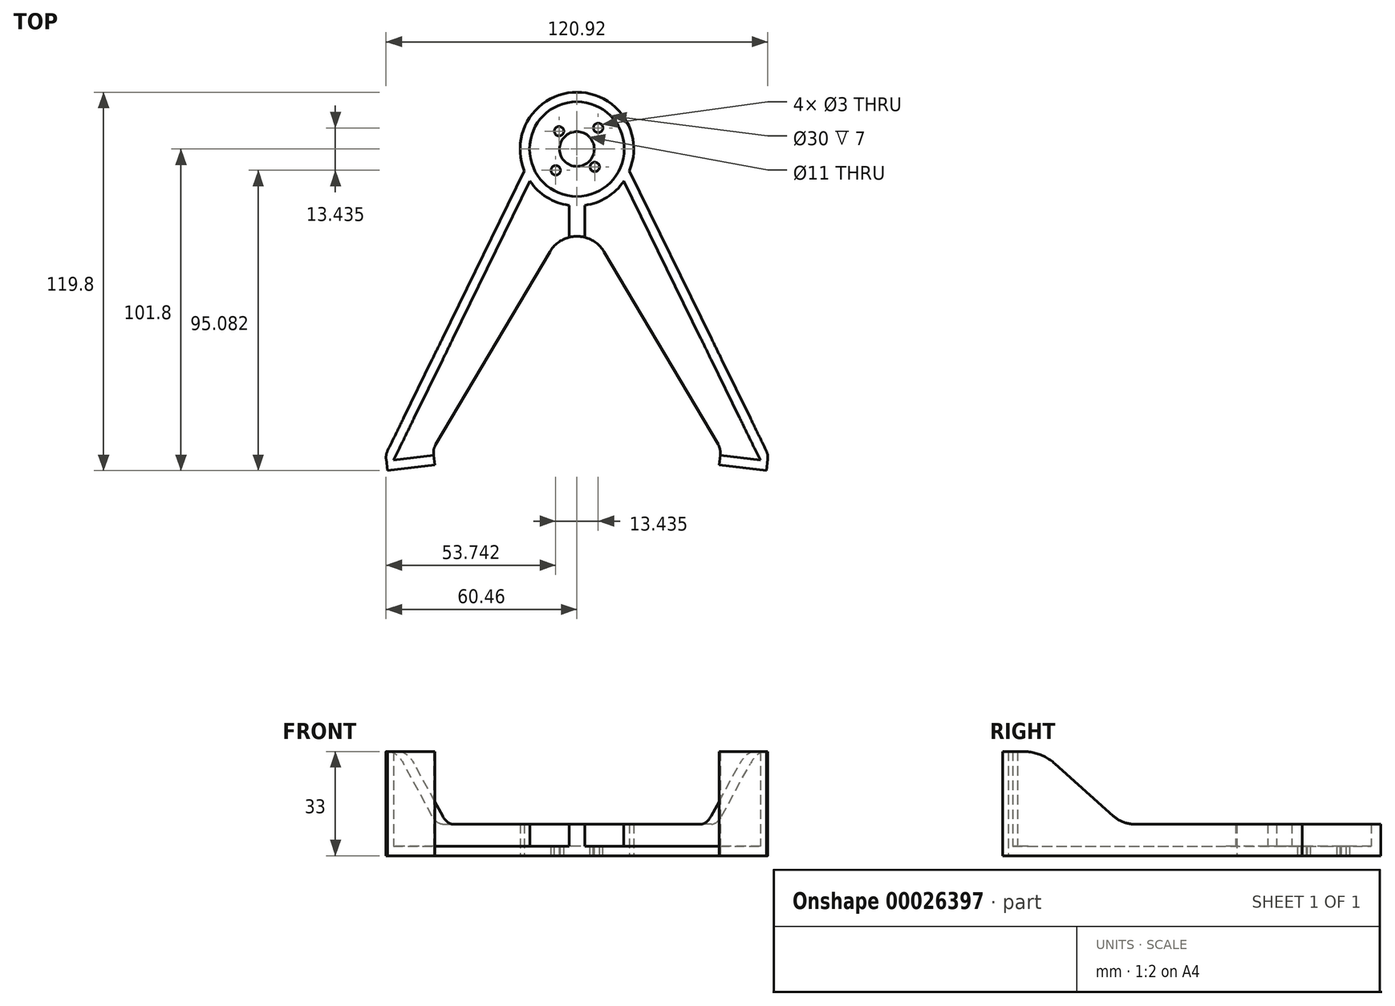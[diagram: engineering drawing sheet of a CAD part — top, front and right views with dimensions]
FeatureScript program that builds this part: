
annotation { "Feature Type Name" : "Feature", "Feature Type Description" : "" }
export const myFeature = defineFeature(function(context is Context, id is Id, definition is map)
    precondition{}
    {
        {
            var Q0;
            Q0=qCreatedBy(makeId("Top.planeOp"),FACE);
            var sketch = newSketch(context, id + "F0", { "sketchPlane" : qUnion([Q0])});
            skLineSegment(sketch, "E0", {"start": v(45, 0) * mm, "end": v(60, -1.8) * mm});
            skCircle(sketch, "E1", {"center": v(0, 100) * mm, "radius": 15 * mm});
            skCircle(sketch, "E2", {"center": v(0, 100) * mm, "radius": 18 * mm});
            skLineSegment(sketch, "E3", {"start": v(60, -1.8) * mm, "end": v(60.42, 1.7) * mm});
            skLineSegment(sketch, "E4", {"start": v(59.95, 4.5) * mm, "end": v(16.63, 93.11) * mm});
            skLineSegment(sketch, "E5", {"start": v(44.73, 6.42) * mm, "end": v(8.6, 67.46) * mm});
            skLineSegment(sketch, "E6.MirrorCS", {"start": v(-45.6, 4.96) * mm, "end": v(-8.6, 67.46) * mm});
            skLineSegment(sketch, "E7.MirrorCS", {"start": v(-45, 0) * mm, "end": v(-60, -1.8) * mm});
            skLineSegment(sketch, "E8.MirrorCS", {"start": v(-60, -1.8) * mm, "end": v(-60.42, 1.7) * mm});
            skLineSegment(sketch, "E9.MirrorCS", {"start": v(-59.95, 4.5) * mm, "end": v(-16.63, 93.11) * mm});
            skArc(sketch, "E10", {"start": v(8.6, 67.46) * mm, "mid": v(0, 72.37) * mm, "end": v(-8.6, 67.46) * mm});
            skPoint(sketch, "E11.orphan", {"position": v(0, 82) * mm});
            skPoint(sketch, "E12.visualSharp", {"position": v(-60.6, 3.16) * mm});
            skArc(sketch, "E12.filletArc", {"start": v(-59.95, 4.5) * mm, "mid": v(-60.39, 3.13) * mm, "end": v(-60.42, 1.7) * mm});
            skPoint(sketch, "E13.visualSharp", {"position": v(60.6, 3.16) * mm});
            skArc(sketch, "E13.filletArc", {"start": v(60.42, 1.7) * mm, "mid": v(60.39, 3.13) * mm, "end": v(59.95, 4.5) * mm});
            skLineSegment(sketch, "E14", {"start": v(45, 0) * mm, "end": v(45.4, 3.28) * mm});
            skPoint(sketch, "E15.visualSharp", {"position": v(45.6, 4.96) * mm});
            skArc(sketch, "E15.filletArc", {"start": v(45.4, 3.28) * mm, "mid": v(45.32, 4.9) * mm, "end": v(44.73, 6.42) * mm});
            skLineSegment(sketch, "E16.MirrorCS", {"start": v(-45, 0) * mm, "end": v(-45.4, 3.28) * mm});
            skArc(sketch, "E17.MirrorCS", {"start": v(-45.4, 3.28) * mm, "mid": v(-45.32, 4.9) * mm, "end": v(-44.73, 6.42) * mm});
            skSolve(sketch);
        }
        {
            var Q0;
            Q0=makeQuery(id+"F0.imprint","IMPRINT",FACE,{"disambiguationData":[TD([[makeQuery(id+"F0.imprint","IMPRINT",EDGE,{"derivedFrom":sQuery(id+"F0.wireOp",EDGE,"E0")}),1.0]])]});
            var Q1;
            Q1=makeQuery(id+"F0.imprint","IMPRINT",FACE,{"disambiguationData":[TD([[makeQuery(id+"F0.imprint","IMPRINT",EDGE,{"derivedFrom":sQuery(id+"F0.wireOp",EDGE,"E1")}),-1.0]])]});
            var Q2;
            Q2=makeQuery(id+"F0.imprint","IMPRINT",FACE,{"disambiguationData":[TD([[makeQuery(id+"F0.imprint","IMPRINT",EDGE,{"derivedFrom":sQuery(id+"F0.wireOp",EDGE,"E1")}),1.0]])]});
            extrude(context, id + "F1", {"entities" : qUnion([Q0, Q1, Q2]), "depth" : 3 * mm});
        }
        {
            var Q0;
            Q0=makeQuery(id+"F0.imprint","IMPRINT",FACE,{"disambiguationData":[TD([[makeQuery(id+"F0.imprint","IMPRINT",EDGE,{"derivedFrom":sQuery(id+"F0.wireOp",EDGE,"E1")}),-1.0]])]});
            extrude(context, id + "F2", {"entities" : qUnion([Q0]), "operationType" : NewBodyOperationType.ADD, "depth" : 10 * mm});
        }
        {
            var Q0;
            {var subQ0=sQuery(id+"F0.wireOp",EDGE,"E10");var subQ1=sQuery(id+"F0.wireOp",EDGE,"E8.MirrorCS");var subQ2=sQuery(id+"F0.wireOp",EDGE,"E16.MirrorCS");var subQ3=sQuery(id+"F0.wireOp",EDGE,"E7.MirrorCS");var subQ4=sQuery(id+"F0.wireOp",EDGE,"E6.MirrorCS");var subQ5=sQuery(id+"F0.wireOp",EDGE,"E5");var subQ6=sQuery(id+"F0.wireOp",EDGE,"E0");var subQ7=sQuery(id+"F0.wireOp",EDGE,"E9.MirrorCS");var subQ8=sQuery(id+"F0.wireOp",EDGE,"E17.MirrorCS");var subQ9=sQuery(id+"F0.wireOp",EDGE,"E2");var subQ10=sQuery(id+"F0.wireOp",EDGE,"E3");var subQ11=sQuery(id+"F0.wireOp",EDGE,"E4");var subQ12=sQuery(id+"F0.wireOp",EDGE,"E12.filletArc");var subQ13=sQuery(id+"F0.wireOp",EDGE,"E13.filletArc");var subQ14=sQuery(id+"F0.wireOp",EDGE,"E14");var subQ15=sQuery(id+"F0.wireOp",EDGE,"E15.filletArc");Q0=makeQuery(id+"F2.boolean.opBoolean","SPLIT",FACE,{"disambiguationData":[TD([makeQuery(id+"F1.opExtrude","SWEPT_FACE",FACE,{"disambiguationData":[OSD([subQ6])]})])],"derivedFrom":makeQuery(id+"F1.opExtrude","CAP_FACE",FACE,{"disambiguationData":[OSD([subQ6,subQ9,subQ10,subQ11,subQ5,subQ4,subQ3,subQ1,subQ7,subQ0,subQ12,subQ13,subQ14,subQ15,subQ2,subQ8])],"isStart":false})});}
            var sketch = newSketch(context, id + "F3", { "sketchPlane" : qUnion([Q0])});
            skLineSegment(sketch, "E18.0", {"start": v(-58.1, 1.45) * mm, "end": v(-14.88, 89.87) * mm});
            skLineSegment(sketch, "E18.1", {"start": v(-45.36, 2.98) * mm, "end": v(-58.1, 1.45) * mm});
            skLineSegment(sketch, "E19", {"start": v(-58.1, 1.45) * mm, "end": v(-60.36, 1.18) * mm});
            skLineSegment(sketch, "E20.MirrorCS", {"start": v(45.36, 2.98) * mm, "end": v(58.1, 1.45) * mm});
            skLineSegment(sketch, "E21.MirrorCS", {"start": v(58.1, 1.45) * mm, "end": v(14.88, 89.87) * mm});
            skLineSegment(sketch, "E22.MirrorCS", {"start": v(58.1, 1.45) * mm, "end": v(60.36, 1.18) * mm});
            skCircle(sketch, "E23.0", {"center": v(0, 100) * mm, "radius": 18 * mm});
            skLineSegment(sketch, "E24.0", {"start": v(-59.95, 4.5) * mm, "end": v(-16.63, 93.11) * mm});
            skArc(sketch, "E25.0", {"start": v(-59.95, 4.5) * mm, "mid": v(-60.39, 3.13) * mm, "end": v(-60.42, 1.7) * mm});
            skLineSegment(sketch, "E26.0", {"start": v(-60, -1.8) * mm, "end": v(-60.42, 1.7) * mm});
            skLineSegment(sketch, "E27.0", {"start": v(-45, 0) * mm, "end": v(-60, -1.8) * mm});
            skLineSegment(sketch, "E28.0", {"start": v(-45, 0) * mm, "end": v(-45.4, 3.28) * mm});
            skLineSegment(sketch, "E29.0", {"start": v(45, 0) * mm, "end": v(45.4, 3.28) * mm});
            skLineSegment(sketch, "E30.0", {"start": v(45, 0) * mm, "end": v(60, -1.8) * mm});
            skLineSegment(sketch, "E31.0", {"start": v(60, -1.8) * mm, "end": v(60.42, 1.7) * mm});
            skArc(sketch, "E32.0", {"start": v(60.42, 1.7) * mm, "mid": v(60.39, 3.13) * mm, "end": v(59.95, 4.5) * mm});
            skLineSegment(sketch, "E33.0", {"start": v(59.95, 4.5) * mm, "end": v(16.63, 93.11) * mm});
            skSolve(sketch);
        }
        {
            var Q0;
            {var subQ2=sQuery(id+"F3.wireOp",EDGE,"E18.0");Q0=makeQuery(id+"F3.imprint","IMPRINT",FACE,{"disambiguationData":[TD([[makeQuery(id+"F3.imprint","IMPRINT",EDGE,{"derivedFrom":subQ2}),1.0]])]});}
            var Q1;
            {var subQ5=sQuery(id+"F3.wireOp",EDGE,"E21.MirrorCS");Q1=makeQuery(id+"F3.imprint","IMPRINT",FACE,{"disambiguationData":[TD([[makeQuery(id+"F3.imprint","IMPRINT",EDGE,{"derivedFrom":subQ5}),-1.0]])]});}
            var Q2;
            Q2=makeQuery(id+"F2.opExtrude","CAP_FACE",FACE,{"disambiguationData":[OSD([sQuery(id+"F0.wireOp",EDGE,"E1"),sQuery(id+"F0.wireOp",EDGE,"E2")])],"isStart":false});
            extrude(context, id + "F4", {"entities" : qUnion([Q0, Q1]), "operationType" : NewBodyOperationType.ADD, "endBound" : BoundingType.UP_TO_SURFACE, "endBoundEntityFace" : qUnion([Q2]), "depth" : 7 * mm});
        }
        {
            var Q0;
            {var subQ3=sQuery(id+"F3.wireOp",EDGE,"E18.1");Q0=makeQuery(id+"F3.imprint","IMPRINT",FACE,{"disambiguationData":[TD([[makeQuery(id+"F3.imprint","IMPRINT",EDGE,{"derivedFrom":subQ3}),1.0]])]});}
            var Q1;
            {var subQ2=sQuery(id+"F3.wireOp",EDGE,"E20.MirrorCS");Q1=makeQuery(id+"F3.imprint","IMPRINT",FACE,{"disambiguationData":[TD([[makeQuery(id+"F3.imprint","IMPRINT",EDGE,{"derivedFrom":subQ2}),-1.0]])]});}
            extrude(context, id + "F5", {"entities" : qUnion([Q0, Q1]), "operationType" : NewBodyOperationType.ADD, "depth" : 30 * mm});
        }
        {
            var Q0;
            {var subQ7=sQuery(id+"F3.wireOp",EDGE,"E18.0");Q0=makeQuery(id+"F3.imprint","IMPRINT",FACE,{"disambiguationData":[TD([[makeQuery(id+"F3.imprint","IMPRINT",EDGE,{"derivedFrom":subQ7}),-1.0]])]});}
            var sketch = newSketch(context, id + "F6", { "sketchPlane" : qUnion([Q0])});
            skArc(sketch, "E34.0", {"start": v(-14.88, 89.87) * mm, "mid": v(0, 82) * mm, "end": v(14.88, 89.87) * mm});
            skArc(sketch, "E35.0", {"start": v(8.6, 67.46) * mm, "mid": v(0, 72.37) * mm, "end": v(-8.6, 67.46) * mm});
            skLineSegment(sketch, "E36", {"start": v(-2.5, 82.17) * mm, "end": v(-2.5, 72.05) * mm});
            skLineSegment(sketch, "E37.MirrorCS", {"start": v(2.5, 82.17) * mm, "end": v(2.5, 72.05) * mm});
            skSolve(sketch);
        }
        {
            var Q0;
            {var subQ0=sQuery(id+"F6.wireOp",EDGE,"E36");Q0=makeQuery(id+"F6.imprint","IMPRINT",FACE,{"disambiguationData":[TD([[makeQuery(id+"F6.imprint","IMPRINT",EDGE,{"derivedFrom":subQ0}),1.0]])]});}
            var Q1;
            {var subQ0=sQuery(id+"F3.wireOp",EDGE,"E23.0");Q1=makeQuery(id+"F4.boolean.opBoolean","MERGE",FACE,{"derivedFrom":[makeQuery(id+"F2.opExtrude","CAP_FACE",FACE,{"disambiguationData":[OSD([sQuery(id+"F0.wireOp",EDGE,"E1"),sQuery(id+"F0.wireOp",EDGE,"E2")])],"isStart":false}),makeQuery(id+"F4.opExtrude","CAP_FACE",FACE,{"disambiguationData":[OSD([sQuery(id+"F3.wireOp",EDGE,"E18.0"),sQuery(id+"F3.wireOp",EDGE,"E19"),subQ0,sQuery(id+"F3.wireOp",EDGE,"E24.0"),sQuery(id+"F3.wireOp",EDGE,"E25.0"),sQuery(id+"F3.wireOp",EDGE,"E26.0")])],"isStart":false}),makeQuery(id+"F4.opExtrude","CAP_FACE",FACE,{"disambiguationData":[OSD([sQuery(id+"F3.wireOp",EDGE,"E21.MirrorCS"),sQuery(id+"F3.wireOp",EDGE,"E22.MirrorCS"),subQ0,sQuery(id+"F3.wireOp",EDGE,"E31.0"),sQuery(id+"F3.wireOp",EDGE,"E32.0"),sQuery(id+"F3.wireOp",EDGE,"E33.0")])],"isStart":false})]});}
            extrude(context, id + "F7", {"entities" : qUnion([Q0]), "operationType" : NewBodyOperationType.ADD, "endBound" : BoundingType.UP_TO_SURFACE, "endBoundEntityFace" : qUnion([Q1]), "depth" : 25 * mm});
        }
        {
            var Q0;
            Q0=makeQuery(id+"F2.boolean.opBoolean","SPLIT",FACE,{"disambiguationData":[TD([makeQuery(id+"F2.opExtrude","SWEPT_FACE",FACE,{"disambiguationData":[OSD([sQuery(id+"F0.wireOp",EDGE,"E1")])]})])],"derivedFrom":makeQuery(id+"F1.opExtrude","CAP_FACE",FACE,{"disambiguationData":[OSD([sQuery(id+"F0.wireOp",EDGE,"E0"),sQuery(id+"F0.wireOp",EDGE,"E2"),sQuery(id+"F0.wireOp",EDGE,"E3"),sQuery(id+"F0.wireOp",EDGE,"E4"),sQuery(id+"F0.wireOp",EDGE,"E5"),sQuery(id+"F0.wireOp",EDGE,"E6.MirrorCS"),sQuery(id+"F0.wireOp",EDGE,"E7.MirrorCS"),sQuery(id+"F0.wireOp",EDGE,"E8.MirrorCS"),sQuery(id+"F0.wireOp",EDGE,"E9.MirrorCS"),sQuery(id+"F0.wireOp",EDGE,"E10"),sQuery(id+"F0.wireOp",EDGE,"E12.filletArc"),sQuery(id+"F0.wireOp",EDGE,"E13.filletArc"),sQuery(id+"F0.wireOp",EDGE,"E14"),sQuery(id+"F0.wireOp",EDGE,"E15.filletArc"),sQuery(id+"F0.wireOp",EDGE,"E16.MirrorCS"),sQuery(id+"F0.wireOp",EDGE,"E17.MirrorCS")])],"isStart":false})});
            var sketch = newSketch(context, id + "F8", { "sketchPlane" : qUnion([Q0])});
            skCircle(sketch, "E38.0", {"center": v(0, 100) * mm, "radius": 15 * mm});
            skCircle(sketch, "E39", {"center": v(0, 100) * mm, "radius": 5.5 * mm});
            skLineSegment(sketch, "E40", {"start": v(-10.6, 89.4) * mm, "end": v(10.6, 110.6) * mm, "construction": true});
            skCircle(sketch, "E41", {"center": v(6.72, 106.72) * mm, "radius": 1.5 * mm});
            skCircle(sketch, "E42", {"center": v(-6.72, 93.28) * mm, "radius": 1.5 * mm});
            skLineSegment(sketch, "E43", {"start": v(-10.6, 110.6) * mm, "end": v(10.6, 89.4) * mm, "construction": true});
            skCircle(sketch, "E44", {"center": v(-5.66, 105.66) * mm, "radius": 1.5 * mm});
            skCircle(sketch, "E45", {"center": v(5.66, 94.34) * mm, "radius": 1.5 * mm});
            skLineSegment(sketch, "E46.0", {"start": v(45.36, 2.98) * mm, "end": v(60.36, 1.18) * mm});
            skLineSegment(sketch, "E47.0", {"start": v(45, 0) * mm, "end": v(60, -1.8) * mm});
            skLineSegment(sketch, "E48.0", {"start": v(58.1, 1.45) * mm, "end": v(14.88, 89.87) * mm});
            skLineSegment(sketch, "E49.MirrorCS", {"start": v(-45.36, 2.98) * mm, "end": v(-60.36, 1.18) * mm});
            skLineSegment(sketch, "E50.MirrorCS", {"start": v(-58.1, 1.45) * mm, "end": v(-14.88, 89.87) * mm});
            skSolve(sketch);
        }
        {
            var Q0;
            Q0=makeQuery(id+"F8.imprint","IMPRINT",FACE,{"disambiguationData":[TD([[makeQuery(id+"F8.imprint","IMPRINT",EDGE,{"derivedFrom":sQuery(id+"F8.wireOp",EDGE,"E39")}),1.0]])]});
            var Q1;
            Q1=makeQuery(id+"F8.imprint","IMPRINT",FACE,{"disambiguationData":[TD([[makeQuery(id+"F8.imprint","IMPRINT",EDGE,{"derivedFrom":sQuery(id+"F8.wireOp",EDGE,"E44")}),1.0]])]});
            var Q2;
            Q2=makeQuery(id+"F8.imprint","IMPRINT",FACE,{"disambiguationData":[TD([[makeQuery(id+"F8.imprint","IMPRINT",EDGE,{"derivedFrom":sQuery(id+"F8.wireOp",EDGE,"E42")}),1.0]])]});
            var Q3;
            Q3=makeQuery(id+"F8.imprint","IMPRINT",FACE,{"disambiguationData":[TD([[makeQuery(id+"F8.imprint","IMPRINT",EDGE,{"derivedFrom":sQuery(id+"F8.wireOp",EDGE,"E45")}),1.0]])]});
            var Q4;
            Q4=makeQuery(id+"F8.imprint","IMPRINT",FACE,{"disambiguationData":[TD([[makeQuery(id+"F8.imprint","IMPRINT",EDGE,{"derivedFrom":sQuery(id+"F8.wireOp",EDGE,"E41")}),1.0]])]});
            var Q5;
            Q5=makeQuery(id+"F1.opExtrude","CAP_FACE",FACE,{"disambiguationData":[OSD([sQuery(id+"F0.wireOp",EDGE,"E0"),sQuery(id+"F0.wireOp",EDGE,"E2"),sQuery(id+"F0.wireOp",EDGE,"E3"),sQuery(id+"F0.wireOp",EDGE,"E4"),sQuery(id+"F0.wireOp",EDGE,"E5"),sQuery(id+"F0.wireOp",EDGE,"E6.MirrorCS"),sQuery(id+"F0.wireOp",EDGE,"E7.MirrorCS"),sQuery(id+"F0.wireOp",EDGE,"E8.MirrorCS"),sQuery(id+"F0.wireOp",EDGE,"E9.MirrorCS"),sQuery(id+"F0.wireOp",EDGE,"E10"),sQuery(id+"F0.wireOp",EDGE,"E12.filletArc"),sQuery(id+"F0.wireOp",EDGE,"E13.filletArc"),sQuery(id+"F0.wireOp",EDGE,"E14"),sQuery(id+"F0.wireOp",EDGE,"E15.filletArc"),sQuery(id+"F0.wireOp",EDGE,"E16.MirrorCS"),sQuery(id+"F0.wireOp",EDGE,"E17.MirrorCS")])],"isStart":true});
            extrude(context, id + "F9", {"entities" : qUnion([Q0, Q1, Q2, Q3, Q4]), "operationType" : NewBodyOperationType.REMOVE, "endBound" : BoundingType.UP_TO_SURFACE, "oppositeDirection" : true, "endBoundEntityFace" : qUnion([Q5]), "depth" : 25 * mm});
        }
        {
            var Q0;
            Q0=makeQuery(id+"F5.opExtrude","CAP_FACE",FACE,{"disambiguationData":[OSD([sQuery(id+"F3.wireOp",EDGE,"E20.MirrorCS"),sQuery(id+"F3.wireOp",EDGE,"E22.MirrorCS"),sQuery(id+"F3.wireOp",EDGE,"E29.0"),sQuery(id+"F3.wireOp",EDGE,"E30.0"),sQuery(id+"F3.wireOp",EDGE,"E31.0")])],"isStart":false});
            var sketch = newSketch(context, id + "F10", { "sketchPlane" : qUnion([Q0])});
            skLineSegment(sketch, "E51.0", {"start": v(45.36, 2.98) * mm, "end": v(60.36, 1.18) * mm});
            skLineSegment(sketch, "E52.0", {"start": v(58.1, 1.45) * mm, "end": v(14.88, 89.87) * mm});
            skLineSegment(sketch, "E53.0", {"start": v(59.95, 4.5) * mm, "end": v(16.63, 93.11) * mm});
            skArc(sketch, "E54.0", {"start": v(60.42, 1.7) * mm, "mid": v(60.39, 3.13) * mm, "end": v(59.95, 4.5) * mm});
            skLineSegment(sketch, "E55.0", {"start": v(60.36, 1.18) * mm, "end": v(60.42, 1.7) * mm});
            skArc(sketch, "E56.0", {"start": v(45.4, 3.28) * mm, "mid": v(45.32, 4.9) * mm, "end": v(44.73, 6.42) * mm});
            skLineSegment(sketch, "E57.0", {"start": v(45.36, 2.98) * mm, "end": v(45.4, 3.28) * mm});
            skLineSegment(sketch, "E58.0", {"start": v(44.73, 6.42) * mm, "end": v(8.6, 67.46) * mm});
            skLineSegment(sketch, "E59", {"start": v(39.25, 40) * mm, "end": v(42.6, 40) * mm});
            skLineSegment(sketch, "E60.MirrorCS", {"start": v(-39.25, 40) * mm, "end": v(-42.6, 40) * mm});
            skLineSegment(sketch, "E61.0", {"start": v(-59.95, 4.5) * mm, "end": v(-16.63, 93.11) * mm});
            skLineSegment(sketch, "E62.0", {"start": v(-58.1, 1.45) * mm, "end": v(-14.88, 89.87) * mm});
            skArc(sketch, "E63.0", {"start": v(-59.95, 4.5) * mm, "mid": v(-60.39, 3.13) * mm, "end": v(-60.42, 1.7) * mm});
            skLineSegment(sketch, "E64.0", {"start": v(-60.36, 1.18) * mm, "end": v(-60.42, 1.7) * mm});
            skLineSegment(sketch, "E65.0", {"start": v(-45.36, 2.98) * mm, "end": v(-60.36, 1.18) * mm});
            skSolve(sketch);
        }
        {
            var Q0;
            {var subQ2=sQuery(id+"F10.wireOp",EDGE,"E60.MirrorCS");Q0=makeQuery(id+"F10.imprint","IMPRINT",FACE,{"disambiguationData":[TD([[makeQuery(id+"F10.imprint","IMPRINT",EDGE,{"derivedFrom":subQ2}),1.0]])]});}
            var Q1;
            {var subQ0=sQuery(id+"F10.wireOp",EDGE,"E54.0");Q1=makeQuery(id+"F10.imprint","IMPRINT",FACE,{"disambiguationData":[TD([[makeQuery(id+"F10.imprint","IMPRINT",EDGE,{"derivedFrom":subQ0}),1.0]])]});}
            var Q2;
            {var subQ0=sQuery(id+"F3.wireOp",EDGE,"E23.0");Q2=makeQuery(id+"F7.boolean.opBoolean","MERGE",FACE,{"derivedFrom":[makeQuery(id+"F4.boolean.opBoolean","MERGE",FACE,{"derivedFrom":[makeQuery(id+"F2.opExtrude","CAP_FACE",FACE,{"disambiguationData":[OSD([sQuery(id+"F0.wireOp",EDGE,"E1"),sQuery(id+"F0.wireOp",EDGE,"E2")])],"isStart":false}),makeQuery(id+"F4.opExtrude","CAP_FACE",FACE,{"disambiguationData":[OSD([sQuery(id+"F3.wireOp",EDGE,"E18.0"),sQuery(id+"F3.wireOp",EDGE,"E19"),subQ0,sQuery(id+"F3.wireOp",EDGE,"E24.0"),sQuery(id+"F3.wireOp",EDGE,"E25.0"),sQuery(id+"F3.wireOp",EDGE,"E26.0")])],"isStart":false}),makeQuery(id+"F4.opExtrude","CAP_FACE",FACE,{"disambiguationData":[OSD([sQuery(id+"F3.wireOp",EDGE,"E21.MirrorCS"),sQuery(id+"F3.wireOp",EDGE,"E22.MirrorCS"),subQ0,sQuery(id+"F3.wireOp",EDGE,"E31.0"),sQuery(id+"F3.wireOp",EDGE,"E32.0"),sQuery(id+"F3.wireOp",EDGE,"E33.0")])],"isStart":false})]}),makeQuery(id+"F7.opExtrude","CAP_FACE",FACE,{"disambiguationData":[OSD([sQuery(id+"F6.wireOp",EDGE,"E34.0"),sQuery(id+"F6.wireOp",EDGE,"E35.0"),sQuery(id+"F6.wireOp",EDGE,"E36"),sQuery(id+"F6.wireOp",EDGE,"E37.MirrorCS")])],"isStart":false})]});}
            extrude(context, id + "F11", {"entities" : qUnion([Q0, Q1]), "operationType" : NewBodyOperationType.ADD, "endBound" : BoundingType.UP_TO_SURFACE, "oppositeDirection" : true, "endBoundEntityFace" : qUnion([Q2]), "depth" : 25 * mm});
        }
        {
            var Q0;
            Q0=qCreatedBy(makeId("Right.planeOp"),FACE);
            var sketch = newSketch(context, id + "F12", { "sketchPlane" : qUnion([Q0])});
            skLineSegment(sketch, "E66.0", {"start": v(40, 10) * mm, "end": v(40, 33) * mm});
            skLineSegment(sketch, "E67.0", {"start": v(4.5, 33) * mm, "end": v(4.79, 33) * mm});
            skLineSegment(sketch, "E68", {"start": v(40, 10) * mm, "end": v(40, 10) * mm});
            skLineSegment(sketch, "E69", {"start": v(33.32, 12.56) * mm, "end": v(14.8, 29.17) * mm});
            skPoint(sketch, "E70.visualSharp", {"position": v(36.17, 10) * mm});
            skArc(sketch, "E70.filletArc", {"start": v(33.32, 12.56) * mm, "mid": v(36.43, 10.66) * mm, "end": v(40, 10) * mm});
            skArc(sketch, "E71.filletArc", {"start": v(14.8, 29.17) * mm, "mid": v(10.15, 32) * mm, "end": v(4.79, 33) * mm});
            skLineSegment(sketch, "E72.0", {"start": v(4.5, 33) * mm, "end": v(40, 33) * mm});
            skSolve(sketch);
        }
        {
            var Q0;
            {var subQ2=sQuery(id+"F12.wireOp",EDGE,"E66.0");Q0=makeQuery(id+"F12.imprint","IMPRINT",FACE,{"disambiguationData":[TD([[makeQuery(id+"F12.imprint","IMPRINT",EDGE,{"derivedFrom":subQ2}),1.0]])]});}
            extrude(context, id + "F13", {"entities" : qUnion([Q0]), "operationType" : NewBodyOperationType.REMOVE, "endBound" : BoundingType.SYMMETRIC, "depth" : 200 * mm});
        }
    });
